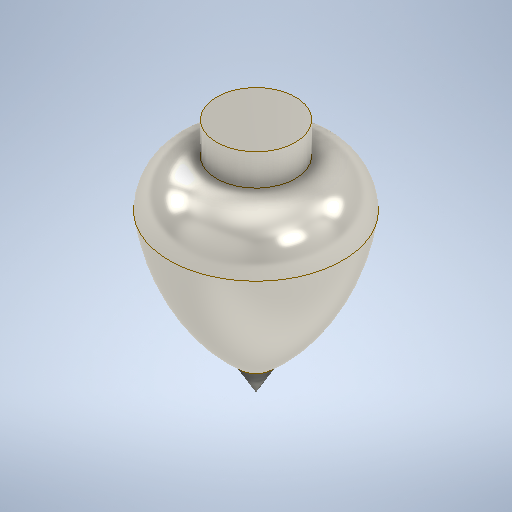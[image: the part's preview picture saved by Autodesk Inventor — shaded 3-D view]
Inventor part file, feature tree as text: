
AUTODESK INVENTOR PART (.ipt)
format: ipt  version: 2025.2 (Build 292293000, 293)  size: 296,960 bytes
history: native  units: mm
features: other x2, sketch x1
ambient origin geometry x8: Origin, YZ Plane, XZ Plane, XY Plane, X Axis, Y Axis, Z Axis, Center Point
bodies: Body1 (feature_tree)
feature tree (3):
  other  "Sólido1"
  other  "Revolução1"
  sketch  "Esboço1"  dims[d0=5.0mm d1=5.0mm d2=2.0mm d3=10.0mm d4=30.0deg d5=2.0mm d7=13.0mm d8=90.0deg]
